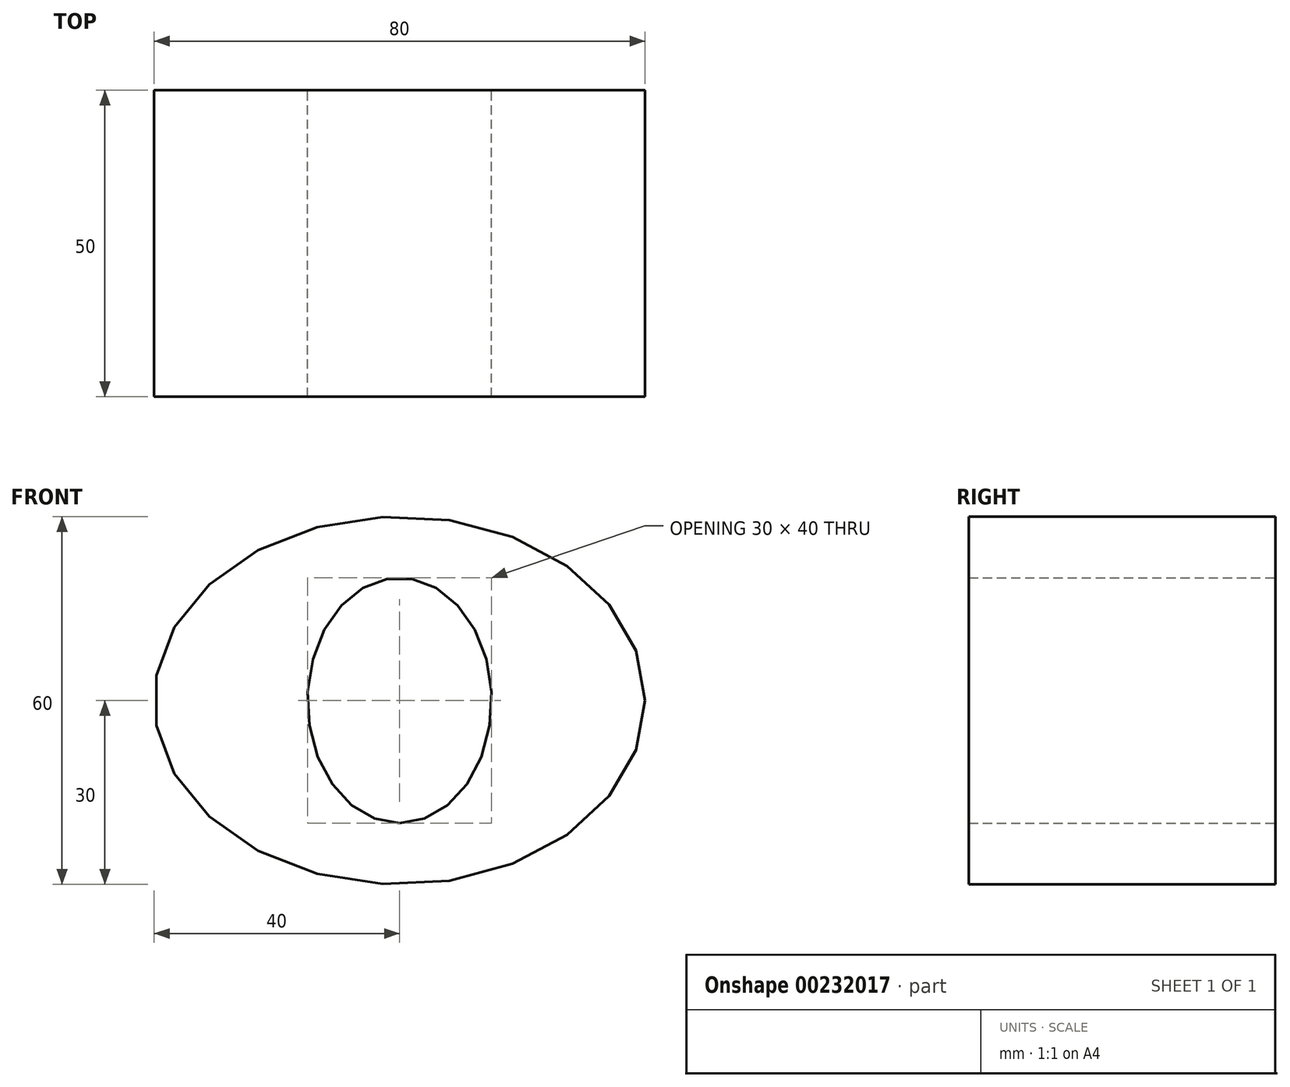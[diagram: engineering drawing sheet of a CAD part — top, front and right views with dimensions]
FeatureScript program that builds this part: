
annotation { "Feature Type Name" : "Feature", "Feature Type Description" : "" }
export const myFeature = defineFeature(function(context is Context, id is Id, definition is map)
    precondition{}
    {
        {
            var Q0;
            Q0=qCreatedBy(makeId("Front.planeOp"),FACE);
            var sketch = newSketch(context, id + "F0", { "sketchPlane" : qUnion([Q0])});
            skEllipse(sketch, "E0", {"center": v(0, 0) * mm, "majorRadius": 40 * mm, "minorRadius": 30 * mm, "majorAxis": v(1, 0)});
            skEllipse(sketch, "E1", {"center": v(0, 0) * mm, "majorRadius": 20 * mm, "minorRadius": 15 * mm, "majorAxis": v(0, -1)});
            skSolve(sketch);
        }
        {
            var Q0;
            Q0 = qSketchRegion(id + "F0", true);
            extrude(context, id + "F1", {"entities" : qUnion([Q0]), "depth" : 50 * mm});
        }
    });
